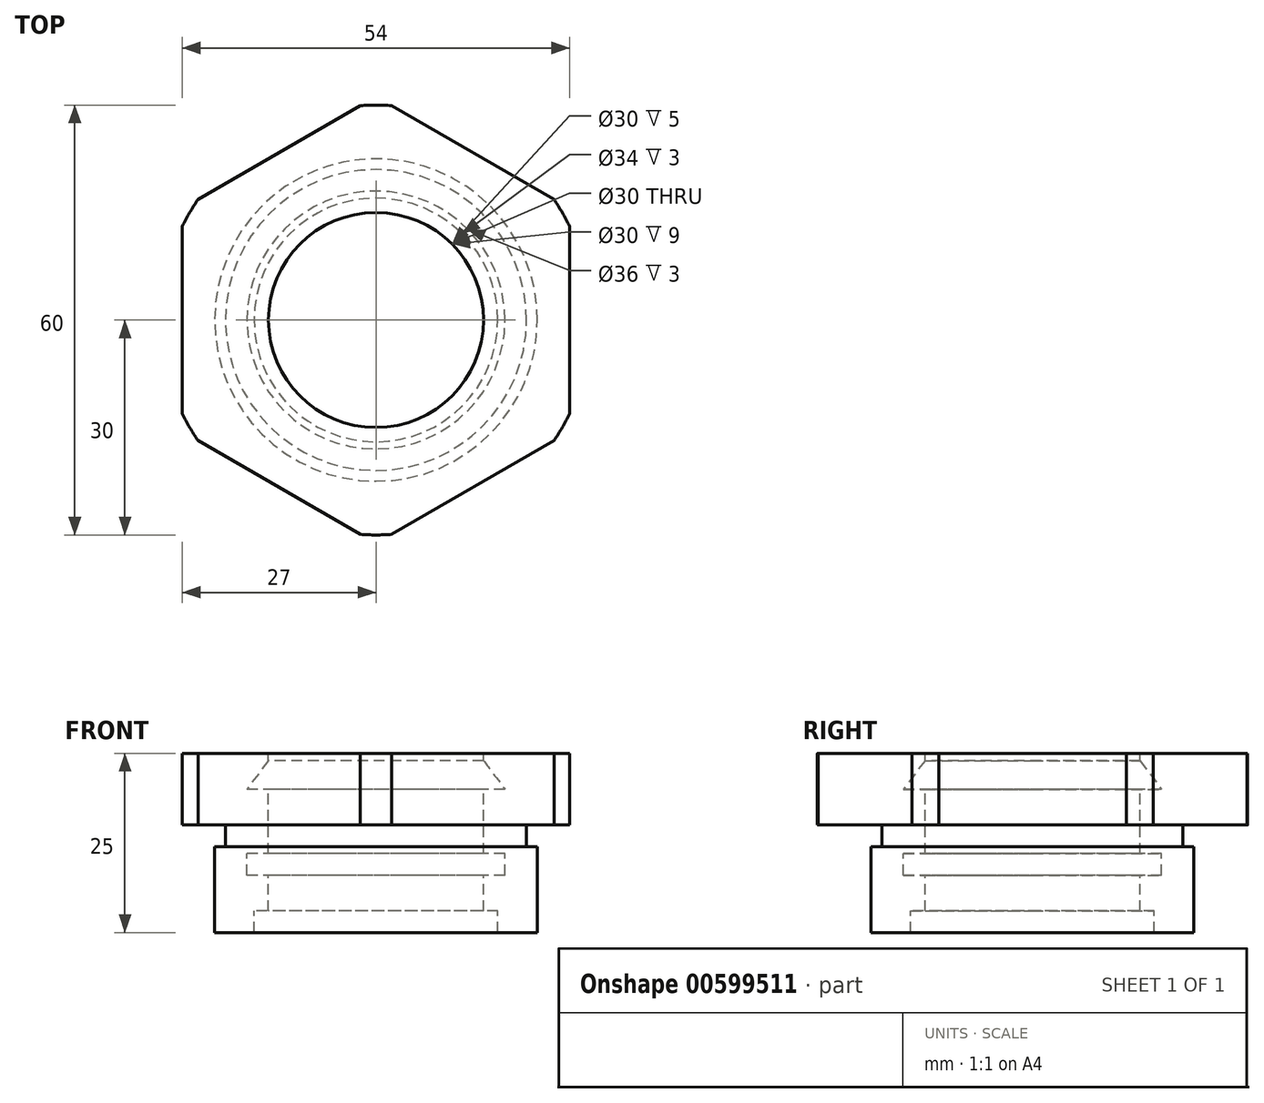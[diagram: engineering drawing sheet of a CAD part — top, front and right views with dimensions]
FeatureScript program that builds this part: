
annotation { "Feature Type Name" : "Feature", "Feature Type Description" : "" }
export const myFeature = defineFeature(function(context is Context, id is Id, definition is map)
    precondition{}
    {
        {
            var Q0;
            Q0=qCreatedBy(makeId("Front.planeOp"),FACE);
            var sketch = newSketch(context, id + "F0", { "sketchPlane" : qUnion([Q0])});
            skLineSegment(sketch, "E0", {"start": v(0, 33.7) * mm, "end": v(0, 0) * mm, "construction": true});
            skLineSegment(sketch, "E1", {"start": v(0, 0) * mm, "end": v(31.65, 0) * mm, "construction": true});
            skLineSegment(sketch, "E2", {"start": v(15, 0) * mm, "end": v(15, 5) * mm});
            skLineSegment(sketch, "E3", {"start": v(15, 5) * mm, "end": v(17, 5) * mm});
            skLineSegment(sketch, "E4", {"start": v(17, 8) * mm, "end": v(15, 8) * mm});
            skLineSegment(sketch, "E5", {"start": v(15, 8) * mm, "end": v(15, 13) * mm});
            skLineSegment(sketch, "E6", {"start": v(15, 13) * mm, "end": v(18, 13) * mm});
            skLineSegment(sketch, "E7", {"start": v(18, 13) * mm, "end": v(18, 16) * mm});
            skLineSegment(sketch, "E8", {"start": v(18, 16) * mm, "end": v(15, 16) * mm});
            skLineSegment(sketch, "E9", {"start": v(15, 16) * mm, "end": v(15, 25) * mm});
            skLineSegment(sketch, "E10", {"start": v(15, 25) * mm, "end": v(18, 25) * mm});
            skLineSegment(sketch, "E11", {"start": v(18, 25) * mm, "end": v(15, 29) * mm});
            skLineSegment(sketch, "E12", {"start": v(15, 29) * mm, "end": v(15, 30) * mm});
            skLineSegment(sketch, "E13", {"start": v(15, 30) * mm, "end": v(30, 30) * mm});
            skLineSegment(sketch, "E14", {"start": v(30, 30) * mm, "end": v(30, 20) * mm});
            skLineSegment(sketch, "E15", {"start": v(30, 20) * mm, "end": v(21, 20) * mm});
            skLineSegment(sketch, "E16", {"start": v(21, 20) * mm, "end": v(21, 17) * mm});
            skLineSegment(sketch, "E17", {"start": v(21, 17) * mm, "end": v(22.5, 17) * mm});
            skLineSegment(sketch, "E18", {"start": v(22.5, 17) * mm, "end": v(22.5, 0) * mm});
            skLineSegment(sketch, "E19", {"start": v(22.5, 0) * mm, "end": v(15, 0) * mm});
            skLineSegment(sketch, "E20", {"start": v(17, 8) * mm, "end": v(17, 5) * mm});
            skSolve(sketch);
        }
        {
            var Q0;
            Q0 = qSketchRegion(id + "F0", true);
            var Q1;
            Q1=sQuery(id+"F0.wireOp",EDGE,"E0");
            revolve(context, id + "F1", {"entities" : qUnion([Q0]), "axis" : qUnion([Q1]), "revolveType" : RevolveType.FULL});
        }
        {
            var Q0;
            Q0=makeQuery(id+"F1.opRevolve","SWEPT_FACE",FACE,{"disambiguationData":[OSD([sQuery(id+"F0.wireOp",EDGE,"E13")])]});
            var sketch = newSketch(context, id + "F2", { "sketchPlane" : qUnion([Q0])});
            skCircle(sketch, "E21.cCircle", {"center": v(0, 0) * mm, "radius": 27 * mm, "construction": true});
            skLineSegment(sketch, "E21.0", {"start": v(27, -15.59) * mm, "end": v(0, -31.18) * mm});
            skLineSegment(sketch, "E21.1", {"start": v(0, -31.18) * mm, "end": v(-27, -15.59) * mm});
            skLineSegment(sketch, "E21.2", {"start": v(-27, -15.59) * mm, "end": v(-27, 15.59) * mm});
            skLineSegment(sketch, "E21.3", {"start": v(-27, 15.59) * mm, "end": v(0, 31.18) * mm});
            skLineSegment(sketch, "E21.4", {"start": v(0, 31.18) * mm, "end": v(27, 15.59) * mm});
            skLineSegment(sketch, "E21.5", {"start": v(27, 15.59) * mm, "end": v(27, -15.59) * mm});
            skPoint(sketch, "E21.0.midPoint", {"position": v(13.5, -23.38) * mm});
            skSolve(sketch);
        }
        {
            var Q0;
            Q0 = qSketchRegion(id + "F2", true);
            extrude(context, id + "F3", {"entities" : qUnion([Q0]), "operationType" : NewBodyOperationType.INTERSECT, "oppositeDirection" : true, "depth" : 25 * mm, "offsetDistance" : 25 * mm});
        }
    });
